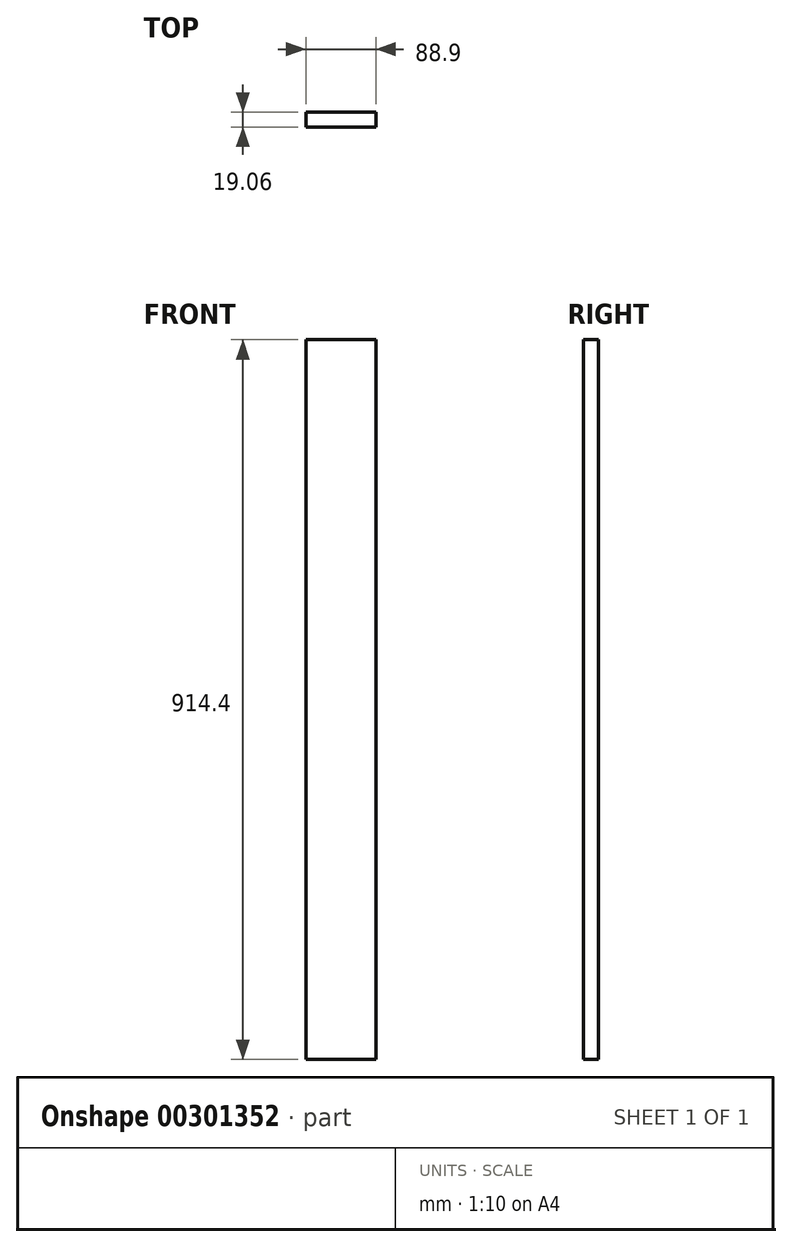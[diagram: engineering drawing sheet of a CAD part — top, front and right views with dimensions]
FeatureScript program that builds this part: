
annotation { "Feature Type Name" : "Feature", "Feature Type Description" : "" }
export const myFeature = defineFeature(function(context is Context, id is Id, definition is map)
    precondition{}
    {
        {
            var Q0;
            Q0=qCreatedBy(makeId("Top.planeOp"),FACE);
            var sketch = newSketch(context, id + "F0", { "sketchPlane" : qUnion([Q0])});
            skLineSegment(sketch, "E0.bottom", {"start": v(44.45, -9.52) * mm, "end": v(-44.45, -9.53) * mm});
            skLineSegment(sketch, "E0.top", {"start": v(44.45, 9.53) * mm, "end": v(-44.45, 9.52) * mm});
            skLineSegment(sketch, "E0.left", {"start": v(44.45, -9.52) * mm, "end": v(44.45, 9.53) * mm});
            skLineSegment(sketch, "E0.right", {"start": v(-44.45, -9.53) * mm, "end": v(-44.45, 9.53) * mm});
            skPoint(sketch, "E0.middle", {"position": v(0, 0) * mm});
            skSolve(sketch);
        }
        {
            var Q0;
            Q0=makeQuery(id+"F0.imprint","IMPRINT",FACE,{"disambiguationData":[TD([[makeQuery(id+"F0.imprint","IMPRINT",EDGE,{"derivedFrom":sQuery(id+"F0.wireOp",EDGE,"E0.bottom")}),-1.0]])]});
            extrude(context, id + "F1", {"entities" : qUnion([Q0]), "endBound" : BoundingType.SYMMETRIC, "depth" : 914.4 * mm});
        }
    });
